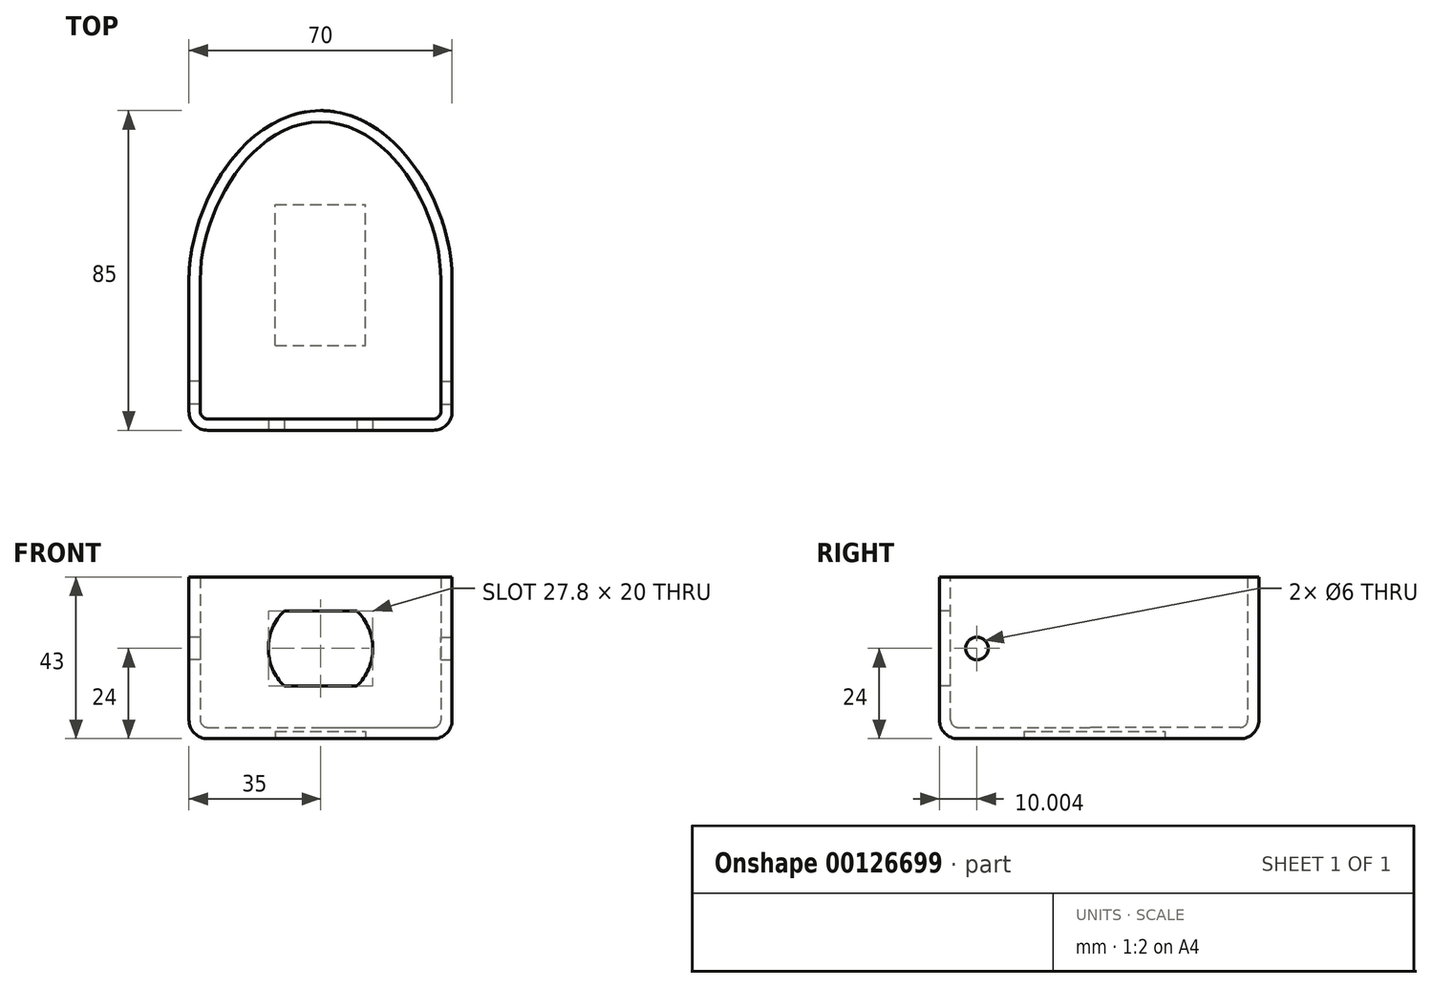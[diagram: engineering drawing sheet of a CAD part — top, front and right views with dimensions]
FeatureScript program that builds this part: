
annotation { "Feature Type Name" : "Feature", "Feature Type Description" : "" }
export const myFeature = defineFeature(function(context is Context, id is Id, definition is map)
    precondition{}
    {
        {
            var Q0;
            Q0=qCreatedBy(makeId("Top.planeOp"),FACE);
            var sketch = newSketch(context, id + "F0", { "sketchPlane" : qUnion([Q0])});
            skLineSegment(sketch, "E0.top", {"start": v(-35, -41.29) * mm, "end": v(35, -41.29) * mm});
            skPoint(sketch, "E0.middle", {"position": v(0, 0) * mm});
            skPoint(sketch, "E1.visualSharp", {"position": v(-35, -41.29) * mm});
            skPoint(sketch, "E2.visualSharp", {"position": v(35, -41.29) * mm});
            skPoint(sketch, "E3", {"position": v(-35, -1.29) * mm});
            skPoint(sketch, "E4", {"position": v(35, -1.29) * mm});
            skLineSegment(sketch, "E5", {"start": v(-35, -1.29) * mm, "end": v(-35, -41.29) * mm});
            skLineSegment(sketch, "E6", {"start": v(35, -1.29) * mm, "end": v(35, -41.29) * mm});
            skFitSpline(sketch, "E7", {"points": [v(0, 43.71) * mm, v(-35, -1.29) * mm], "startDerivative": vector(-60.6, 0) * mm, "endDerivative": vector(0, -60.15) * mm});
            skFitSpline(sketch, "E8.MirrorCS", {"points": [v(0, 43.71) * mm, v(35, -1.29) * mm], "startDerivative": vector(60.6, 0) * mm, "endDerivative": vector(0, -60.15) * mm});
            skSolve(sketch);
        }
        {
            var Q0;
            Q0=qSketchRegion(id+"F0",true);
            extrude(context, id + "F1", {"entities" : qUnion([Q0]), "endBound" : BoundingType.SYMMETRIC, "depth" : 48 * mm});
        }
        {
            var Q0;
            Q0=qCreatedBy(makeId("Right.planeOp"),FACE);
            var sketch = newSketch(context, id + "F2", { "sketchPlane" : qUnion([Q0])});
            skLineSegment(sketch, "E9", {"start": v(0, 0) * mm, "end": v(-30, 0) * mm});
            skPoint(sketch, "E10", {"position": v(-30, 0) * mm});
            skLineSegment(sketch, "E11", {"start": v(-30, 12.5) * mm, "end": v(-30, -12.5) * mm});
            skLineSegment(sketch, "E12", {"start": v(-30, -12.5) * mm, "end": v(0, -12.5) * mm});
            skLineSegment(sketch, "E13", {"start": v(-30, 12.5) * mm, "end": v(-15.57, -12.5) * mm});
            skLineSegment(sketch, "E14", {"start": v(-30, 7.5) * mm, "end": v(-27.11, 7.5) * mm});
            skLineSegment(sketch, "E15.bottom", {"start": v(-30, 7.5) * mm, "end": v(-40, 7.5) * mm});
            skLineSegment(sketch, "E15.top", {"start": v(-30, -12.5) * mm, "end": v(-40, -12.5) * mm});
            skLineSegment(sketch, "E15.left", {"start": v(-30, 7.5) * mm, "end": v(-30, -12.5) * mm});
            skLineSegment(sketch, "E15.right", {"start": v(-40, 7.5) * mm, "end": v(-40, -12.5) * mm});
            skSolve(sketch);
        }
        {
            var Q0;
            Q0=makeQuery(id+"F1.opExtrude","CAP_FACE",FACE,{"disambiguationData":[OSD([sQuery(id+"F0.wireOp",EDGE,"E0.top"),sQuery(id+"F0.wireOp",EDGE,"49a04736-c9a8-4021-8eca-e335ee950ef4"),sQuery(id+"F0.wireOp",EDGE,"5cda4a63-8e27-4d9c-be18-28a9360ed2950.MirrorCS"),sQuery(id+"F0.wireOp",EDGE,"E5"),sQuery(id+"F0.wireOp",EDGE,"E6")])],"isStart":true});
            var sketch = newSketch(context, id + "F3", { "sketchPlane" : qUnion([Q0])});
            skLineSegment(sketch, "E16.bottom", {"start": v(35, 41.29) * mm, "end": v(-25, 41.29) * mm});
            skLineSegment(sketch, "E16.top", {"start": v(35, 56.85) * mm, "end": v(-25, 56.85) * mm});
            skLineSegment(sketch, "E16.left", {"start": v(35, 41.29) * mm, "end": v(35, 56.85) * mm});
            skLineSegment(sketch, "E16.right", {"start": v(-25, 41.29) * mm, "end": v(-25, 56.85) * mm});
            skFitSpline(sketch, "E17", {"points": [v(0, -40) * mm, v(30, 0) * mm], "startDerivative": vector(49.89, 0) * mm, "endDerivative": vector(0, 60.15) * mm});
            skFitSpline(sketch, "E18.MirrorCS", {"points": [v(0, -40) * mm, v(-30, 0) * mm], "startDerivative": vector(-49.89, 0) * mm, "endDerivative": vector(0, 60.15) * mm});
            skFitSpline(sketch, "E19.0", {"points": [v(0, -32) * mm, v(0.64, -32) * mm, v(1.9, -31.9) * mm, v(3.77, -31.49) * mm, v(5.66, -30.78) * mm, v(8.18, -29.45) * mm, v(11.32, -27.03) * mm, v(14.84, -22.99) * mm, v(17.86, -18) * mm, v(20.18, -12.32) * mm, v(21.66, -6.22) * mm, v(22, -2.06) * mm, v(22, 0) * mm]});
            skFitSpline(sketch, "E19.1", {"points": [v(0, -32) * mm, v(-0.64, -32) * mm, v(-1.9, -31.9) * mm, v(-3.77, -31.49) * mm, v(-5.66, -30.78) * mm, v(-8.18, -29.45) * mm, v(-11.32, -27.03) * mm, v(-14.84, -22.99) * mm, v(-17.86, -18) * mm, v(-20.18, -12.32) * mm, v(-21.66, -6.22) * mm, v(-22, -2.06) * mm, v(-22, 0) * mm]});
            skFitSpline(sketch, "E20.0", {"points": [v(0, -27) * mm, v(0.4, -27) * mm, v(1.15, -26.94) * mm, v(2.33, -26.68) * mm, v(3.59, -26.21) * mm, v(4.94, -25.5) * mm, v(6.36, -24.53) * mm, v(8.32, -22.85) * mm, v(10.76, -20.06) * mm, v(13.36, -15.76) * mm, v(15.4, -10.78) * mm, v(16.7, -5.42) * mm, v(17, -1.78) * mm, v(17, 0) * mm]});
            skFitSpline(sketch, "E20.1", {"points": [v(0, -27) * mm, v(-0.4, -27) * mm, v(-1.15, -26.94) * mm, v(-2.33, -26.68) * mm, v(-3.59, -26.21) * mm, v(-4.94, -25.5) * mm, v(-6.36, -24.53) * mm, v(-8.32, -22.85) * mm, v(-10.76, -20.06) * mm, v(-13.36, -15.76) * mm, v(-15.4, -10.78) * mm, v(-16.7, -5.42) * mm, v(-17, -1.78) * mm, v(-17, 0) * mm]});
            skLineSegment(sketch, "E21.bottom", {"start": v(-22, 0) * mm, "end": v(22, 0) * mm});
            skLineSegment(sketch, "E21.top", {"start": v(-22, 10) * mm, "end": v(22, 10) * mm});
            skLineSegment(sketch, "E21.left", {"start": v(-22, 0) * mm, "end": v(-22, 10) * mm});
            skLineSegment(sketch, "E21.right", {"start": v(22, 0) * mm, "end": v(22, 10) * mm});
            skLineSegment(sketch, "E22", {"start": v(-20.56, -10.51) * mm, "end": v(-15.34, -10.51) * mm});
            skLineSegment(sketch, "E23.MirrorCS", {"start": v(20.56, -10.51) * mm, "end": v(15.34, -10.51) * mm});
            skLineSegment(sketch, "E24.top", {"start": v(-22, 5) * mm, "end": v(22, 5) * mm});
            skLineSegment(sketch, "E24.left", {"start": v(-22, 10) * mm, "end": v(-22, 5) * mm});
            skLineSegment(sketch, "E24.right", {"start": v(22, 10) * mm, "end": v(22, 5) * mm});
            skSolve(sketch);
        }
        {
            var Q0;
            Q0=makeQuery(id+"F1.opExtrude","CAP_EDGE",EDGE,{"disambiguationData":[OSD([sQuery(id+"F0.wireOp",EDGE,"E5")])],"isStart":true});
            var Q1;
            Q1=makeQuery(id+"F1.opExtrude","CAP_EDGE",EDGE,{"disambiguationData":[OSD([sQuery(id+"F0.wireOp",EDGE,"E7")])],"isStart":true});
            var Q2;
            Q2=makeQuery(id+"F1.opExtrude","CAP_EDGE",EDGE,{"disambiguationData":[OSD([sQuery(id+"F0.wireOp",EDGE,"E0.top")])],"isStart":false});
            var Q3;
            Q3=makeQuery(id+"F1.opExtrude","CAP_EDGE",EDGE,{"disambiguationData":[OSD([sQuery(id+"F0.wireOp",EDGE,"E5")])],"isStart":false});
            var Q4;
            Q4=makeQuery(id+"F1.opExtrude","SWEPT_EDGE",EDGE,{"disambiguationData":[OSD([sQuery(id+"F0.wireOp",EDGE,"E0.top"),sQuery(id+"F0.wireOp",EDGE,"E5")])]});
            var Q5;
            Q5=makeQuery(id+"F1.opExtrude","SWEPT_EDGE",EDGE,{"disambiguationData":[OSD([sQuery(id+"F0.wireOp",EDGE,"E0.top"),sQuery(id+"F0.wireOp",EDGE,"E6")])]});
            var Q6;
            {var subQ0=sQuery(id+"F0.wireOp",EDGE,"E0.top");var subQ1=sQuery(id+"F0.wireOp",EDGE,"E5");Q6=makeQuery(id+"FKo57LURMALH3DB_1.boolean.opBoolean","SPLIT",EDGE,{"disambiguationData":[TD([makeQuery(id+"F1.opExtrude","SWEPT_FACE",FACE,{"disambiguationData":[OSD([subQ1])]})])],"derivedFrom":makeQuery(id+"F1.opExtrude","CAP_EDGE",EDGE,{"disambiguationData":[OSD([subQ0])],"isStart":true})});}
            var Q7;
            {var subQ0=sQuery(id+"F0.wireOp",EDGE,"E0.top");var subQ1=sQuery(id+"F0.wireOp",EDGE,"E6");Q7=makeQuery(id+"FKo57LURMALH3DB_1.boolean.opBoolean","SPLIT",EDGE,{"disambiguationData":[TD([makeQuery(id+"F1.opExtrude","SWEPT_FACE",FACE,{"disambiguationData":[OSD([subQ1])]})])],"derivedFrom":makeQuery(id+"F1.opExtrude","CAP_EDGE",EDGE,{"disambiguationData":[OSD([subQ0])],"isStart":true})});}
            fillet(context, id + "F4", {"entities" : qUnion([Q0, Q1, Q2, Q3, Q4, Q5, Q6, Q7]), "radius" : 5 * mm, "tangentPropagation" : true, "allowEdgeOverflow" : false});
        }
        {
            var Q0;
            Q0=makeQuery(id+"F1.opExtrude","CAP_FACE",FACE,{"disambiguationData":[OSD([sQuery(id+"F0.wireOp",EDGE,"E0.top"),sQuery(id+"F0.wireOp",EDGE,"E5"),sQuery(id+"F0.wireOp",EDGE,"E6"),sQuery(id+"F0.wireOp",EDGE,"E7"),sQuery(id+"F0.wireOp",EDGE,"E8.MirrorCS")])],"isStart":false});
            var sketch = newSketch(context, id + "F5", { "sketchPlane" : qUnion([Q0])});
            skLineSegment(sketch, "E25.bottom", {"start": v(-45.63, 73.42) * mm, "end": v(45.63, 73.42) * mm});
            skLineSegment(sketch, "E25.top", {"start": v(-45.63, -73.42) * mm, "end": v(45.63, -73.42) * mm});
            skLineSegment(sketch, "E25.left", {"start": v(-45.63, 73.42) * mm, "end": v(-45.63, -73.42) * mm});
            skLineSegment(sketch, "E25.right", {"start": v(45.63, 73.42) * mm, "end": v(45.63, -73.42) * mm});
            skPoint(sketch, "E25.middle", {"position": v(0, 0) * mm});
            skSolve(sketch);
        }
        {
            var Q0;
            Q0=qSketchRegion(id+"F5",true);
            extrude(context, id + "F6", {"entities" : qUnion([Q0]), "operationType" : NewBodyOperationType.REMOVE, "oppositeDirection" : true, "depth" : 5 * mm});
        }
        {
            var Q0;
            Q0=makeQuery(id+"F6.boolean.opBoolean","COPY",FACE,{"derivedFrom":makeQuery(id+"F6.opExtrude","CAP_FACE",FACE,{"disambiguationData":[OSD([sQuery(id+"F5.wireOp",EDGE,"E25.bottom"),sQuery(id+"F5.wireOp",EDGE,"E25.top"),sQuery(id+"F5.wireOp",EDGE,"E25.left"),sQuery(id+"F5.wireOp",EDGE,"E25.right")])],"isStart":false})});
            shell(context, id + "F7", {"entities" : qUnion([Q0]), "thickness" : 3 * mm});
        }
        {
            var Q0;
            Q0=makeQuery(id+"F1.opExtrude","SWEPT_FACE",FACE,{"disambiguationData":[OSD([sQuery(id+"F0.wireOp",EDGE,"E0.top")])]});
            var sketch = newSketch(context, id + "F8", { "sketchPlane" : qUnion([Q0])});
            skLineSegment(sketch, "E26.bottom", {"start": v(-30, 19) * mm, "end": v(30, 19) * mm});
            skLineSegment(sketch, "E26.top", {"start": v(-30, -19) * mm, "end": v(30, -19) * mm});
            skLineSegment(sketch, "E26.left", {"start": v(-30, 19) * mm, "end": v(-30, -19) * mm});
            skLineSegment(sketch, "E26.right", {"start": v(30, 19) * mm, "end": v(30, -19) * mm});
            skPoint(sketch, "E27", {"position": v(0, 0) * mm});
            skPoint(sketch, "E28", {"position": v(-17.5, 0) * mm});
            skPoint(sketch, "E29", {"position": v(17.5, 0) * mm});
            skArc(sketch, "E30", {"start": v(-9.65, 10) * mm, "mid": v(-13.9, 0) * mm, "end": v(-9.65, -10) * mm});
            skLineSegment(sketch, "E31", {"start": v(0, 0) * mm, "end": v(0, 10) * mm});
            skLineSegment(sketch, "E32", {"start": v(0, 0) * mm, "end": v(0, -10) * mm});
            skPoint(sketch, "E32.endSnap0", {"position": v(0, -19) * mm});
            skLineSegment(sketch, "E33", {"start": v(-9.65, 10) * mm, "end": v(9.65, 10) * mm});
            skLineSegment(sketch, "E34", {"start": v(-9.65, -10) * mm, "end": v(9.65, -10) * mm});
            skArc(sketch, "E35.trimOffspring", {"start": v(9.65, -10) * mm, "mid": v(13.9, 0) * mm, "end": v(9.65, 10) * mm});
            skPoint(sketch, "E36.orphan", {"position": v(0, -13.9) * mm});
            skSolve(sketch);
        }
        {
            var Q0;
            Q0=makeQuery(id+"F1.opExtrude","CAP_FACE",FACE,{"disambiguationData":[OSD([sQuery(id+"F0.wireOp",EDGE,"E0.top"),sQuery(id+"F0.wireOp",EDGE,"E5"),sQuery(id+"F0.wireOp",EDGE,"E6"),sQuery(id+"F0.wireOp",EDGE,"E7"),sQuery(id+"F0.wireOp",EDGE,"E8.MirrorCS")])],"isStart":true});
            var sketch = newSketch(context, id + "F9", { "sketchPlane" : qUnion([Q0])});
            skLineSegment(sketch, "E37.bottom", {"start": v(-12, 18.75) * mm, "end": v(12, 18.75) * mm});
            skLineSegment(sketch, "E37.top", {"start": v(-12, -18.75) * mm, "end": v(12, -18.75) * mm});
            skLineSegment(sketch, "E37.left", {"start": v(-12, 18.75) * mm, "end": v(-12, -18.75) * mm});
            skLineSegment(sketch, "E37.right", {"start": v(12, 18.75) * mm, "end": v(12, -18.75) * mm});
            skPoint(sketch, "E38", {"position": v(0, 0) * mm});
            skPoint(sketch, "E38.positionSnap0", {"position": v(0, 18.75) * mm});
            skPoint(sketch, "E38.positionSnap1", {"position": v(-12, 0) * mm});
            skSolve(sketch);
        }
        {
            var Q0;
            Q0=qSketchRegion(id+"F9",true);
            extrude(context, id + "F10", {"entities" : qUnion([Q0]), "operationType" : NewBodyOperationType.REMOVE, "oppositeDirection" : true, "depth" : 2 * mm});
        }
        {
            var Q0;
            {var subQ2=sQuery(id+"F8.wireOp",EDGE,"E31");Q0=makeQuery(id+"F8.imprint","IMPRINT",FACE,{"disambiguationData":[TD([[makeQuery(id+"F8.imprint","IMPRINT",EDGE,{"derivedFrom":subQ2}),-1.0]])]});}
            var Q1;
            {var subQ2=sQuery(id+"F8.wireOp",EDGE,"E30");Q1=makeQuery(id+"F8.imprint","IMPRINT",FACE,{"disambiguationData":[TD([[makeQuery(id+"F8.imprint","IMPRINT",EDGE,{"derivedFrom":subQ2}),1.0]])]});}
            extrude(context, id + "F11", {"entities" : qUnion([Q0, Q1]), "operationType" : NewBodyOperationType.REMOVE, "oppositeDirection" : true, "depth" : 3 * mm});
        }
        {
            var Q0;
            Q0=makeQuery(id+"F6.boolean.opBoolean","COPY",FACE,{"derivedFrom":makeQuery(id+"F6.opExtrude","CAP_FACE",FACE,{"disambiguationData":[OSD([sQuery(id+"F5.wireOp",EDGE,"E25.bottom"),sQuery(id+"F5.wireOp",EDGE,"E25.top"),sQuery(id+"F5.wireOp",EDGE,"E25.left"),sQuery(id+"F5.wireOp",EDGE,"E25.right")])],"isStart":false})});
            var sketch = newSketch(context, id + "F12", { "sketchPlane" : qUnion([Q0])});
            skLineSegment(sketch, "E39.bottom", {"start": v(-13, 36.57) * mm, "end": v(0, 36.57) * mm});
            skLineSegment(sketch, "E39.top", {"start": v(-13, 43.71) * mm, "end": v(0, 43.71) * mm});
            skLineSegment(sketch, "E39.left", {"start": v(-13, 36.57) * mm, "end": v(-13, 43.71) * mm});
            skLineSegment(sketch, "E39.right", {"start": v(0, 36.57) * mm, "end": v(0, 43.71) * mm});
            skLineSegment(sketch, "E40.bottom", {"start": v(0, 43.71) * mm, "end": v(13, 43.71) * mm});
            skLineSegment(sketch, "E40.top", {"start": v(0, 36.57) * mm, "end": v(13, 36.57) * mm});
            skLineSegment(sketch, "E40.left", {"start": v(0, 43.71) * mm, "end": v(0, 36.57) * mm});
            skLineSegment(sketch, "E40.right", {"start": v(13, 43.71) * mm, "end": v(13, 36.57) * mm});
            skSolve(sketch);
        }
        {
            var Q0;
            Q0=makeQuery(id+"F1.opExtrude","SWEPT_FACE",FACE,{"disambiguationData":[OSD([sQuery(id+"F0.wireOp",EDGE,"E5")])]});
            var sketch = newSketch(context, id + "F13", { "sketchPlane" : qUnion([Q0])});
            skCircle(sketch, "E41", {"center": v(31.29, 0) * mm, "radius": 3 * mm});
            skSolve(sketch);
        }
        {
            var Q0;
            Q0=makeQuery(id+"F1.opExtrude","SWEPT_FACE",FACE,{"disambiguationData":[OSD([sQuery(id+"F0.wireOp",EDGE,"E6")])]});
            var sketch = newSketch(context, id + "F14", { "sketchPlane" : qUnion([Q0])});
            skCircle(sketch, "E42", {"center": v(-31.29, 0) * mm, "radius": 3 * mm});
            skSolve(sketch);
        }
        {
            var Q0;
            Q0=qSketchRegion(id+"F13",true);
            extrude(context, id + "F15", {"entities" : qUnion([Q0]), "operationType" : NewBodyOperationType.REMOVE, "oppositeDirection" : true, "depth" : 3 * mm});
        }
        {
            var Q0;
            Q0=makeQuery(id+"F14.imprint","IMPRINT",FACE,{"disambiguationData":[TD([[makeQuery(id+"F14.imprint","IMPRINT",EDGE,{"derivedFrom":sQuery(id+"F14.wireOp",EDGE,"E42")}),1.0]])]});
            extrude(context, id + "F16", {"entities" : qUnion([Q0]), "operationType" : NewBodyOperationType.REMOVE, "oppositeDirection" : true, "depth" : 3 * mm});
        }
    });
